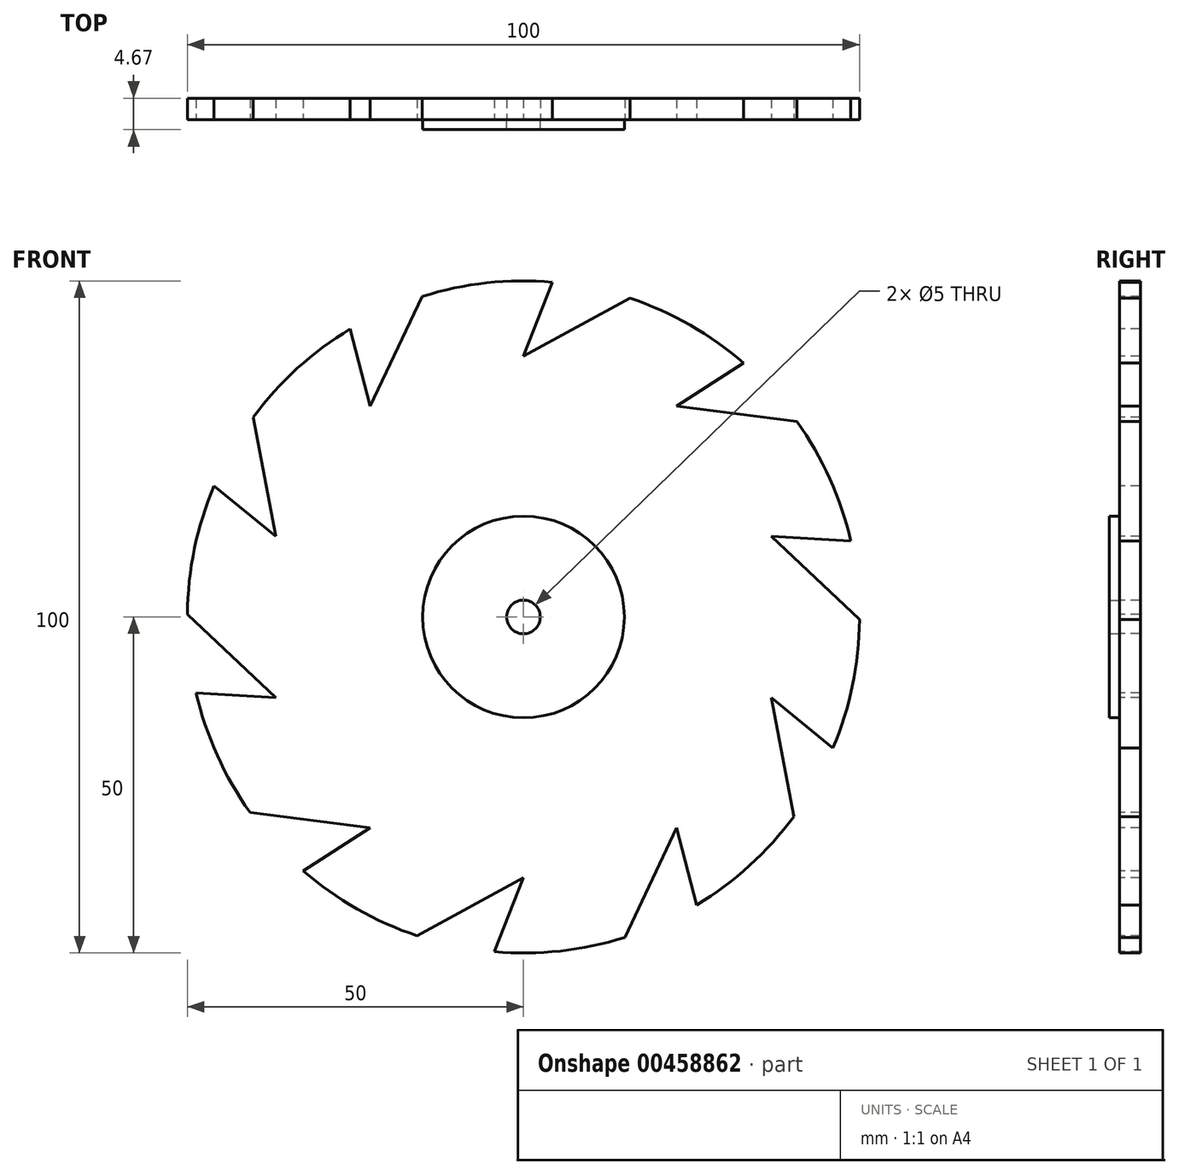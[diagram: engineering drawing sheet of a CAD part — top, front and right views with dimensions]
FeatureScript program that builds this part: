
annotation { "Feature Type Name" : "Feature", "Feature Type Description" : "" }
export const myFeature = defineFeature(function(context is Context, id is Id, definition is map)
    precondition{}
    {
        {
            var Q0;
            Q0=qCreatedBy(makeId("Front.planeOp"),FACE);
            var sketch = newSketch(context, id + "F0", { "sketchPlane" : qUnion([Q0])});
            skCircle(sketch, "E0", {"center": v(0, 0) * mm, "radius": 50 * mm});
            skSolve(sketch);
        }
        {
            var Q0;
            Q0=makeQuery(id+"F0.imprint","IMPRINT",FACE,{"disambiguationData":[TD([[makeQuery(id+"F0.imprint","IMPRINT",EDGE,{"derivedFrom":sQuery(id+"F0.wireOp",EDGE,"E0")}),1.0]])]});
            extrude(context, id + "F1", {"entities" : qUnion([Q0]), "depth" : 3.17 * mm, "offsetDistance" : 25 * mm});
        }
        {
            var Q0;
            Q0=makeQuery(id+"F1.opExtrude","CAP_FACE",FACE,{"disambiguationData":[OSD([sQuery(id+"F0.wireOp",EDGE,"E0")])],"isStart":false});
            var sketch = newSketch(context, id + "F2", { "sketchPlane" : qUnion([Q0])});
            skCircle(sketch, "E1", {"center": v(0, 0) * mm, "radius": 2.5 * mm});
            skSolve(sketch);
        }
        {
            var Q0;
            Q0=makeQuery(id+"F2.imprint","IMPRINT",FACE,{"disambiguationData":[TD([[makeQuery(id+"F2.imprint","IMPRINT",EDGE,{"derivedFrom":sQuery(id+"F2.wireOp",EDGE,"E1")}),1.0]])]});
            extrude(context, id + "F3", {"entities" : qUnion([Q0]), "operationType" : NewBodyOperationType.REMOVE, "oppositeDirection" : true, "depth" : 25 * mm, "offsetDistance" : 25 * mm});
        }
        {
            var Q0;
            Q0=makeQuery(id+"F1.opExtrude","CAP_FACE",FACE,{"disambiguationData":[OSD([sQuery(id+"F0.wireOp",EDGE,"E0")])],"isStart":false});
            var sketch = newSketch(context, id + "F4", { "sketchPlane" : qUnion([Q0])});
            skCircle(sketch, "E2", {"center": v(0, 0) * mm, "radius": 15 * mm});
            skSolve(sketch);
        }
        {
            var Q0;
            Q0=makeQuery(id+"F4.imprint","IMPRINT",FACE,{"disambiguationData":[TD([[makeQuery(id+"F4.imprint","IMPRINT",EDGE,{"derivedFrom":sQuery(id+"F4.wireOp",EDGE,"E2")}),1.0]])]});
            extrude(context, id + "F5", {"entities" : qUnion([Q0]), "depth" : 1.5 * mm, "offsetDistance" : 25 * mm});
        }
        {
            var Q0;
            Q0=makeQuery(id+"F1.opExtrude","CAP_FACE",FACE,{"disambiguationData":[OSD([sQuery(id+"F0.wireOp",EDGE,"E0")])],"isStart":false});
            var sketch = newSketch(context, id + "F6", { "sketchPlane" : qUnion([Q0])});
            skLineSegment(sketch, "E3", {"start": v(15.84, 47.43) * mm, "end": v(0, 38.78) * mm});
            skLineSegment(sketch, "E4", {"start": v(0, 38.78) * mm, "end": v(4.31, 49.81) * mm});
            skLineSegment(sketch, "E5.1.0", {"start": v(-15.06, 47.68) * mm, "end": v(-22.8, 31.37) * mm});
            skLineSegment(sketch, "E5.1.1", {"start": v(-22.8, 31.37) * mm, "end": v(-25.79, 42.84) * mm});
            skLineSegment(sketch, "E5.2.0", {"start": v(-40.2, 29.72) * mm, "end": v(-36.88, 11.98) * mm});
            skLineSegment(sketch, "E5.2.1", {"start": v(-36.88, 11.98) * mm, "end": v(-46.04, 19.5) * mm});
            skLineSegment(sketch, "E5.3.0", {"start": v(-50, 0.4) * mm, "end": v(-36.88, -11.98) * mm});
            skLineSegment(sketch, "E5.3.1", {"start": v(-36.88, -11.98) * mm, "end": v(-48.7, -11.29) * mm});
            skLineSegment(sketch, "E5.4.0", {"start": v(-40.69, -29.06) * mm, "end": v(-22.8, -31.37) * mm});
            skLineSegment(sketch, "E5.4.1", {"start": v(-22.8, -31.37) * mm, "end": v(-32.77, -37.76) * mm});
            skLineSegment(sketch, "E5.5.0", {"start": v(-15.84, -47.43) * mm, "end": v(0, -38.78) * mm});
            skLineSegment(sketch, "E5.5.1", {"start": v(0, -38.78) * mm, "end": v(-4.31, -49.81) * mm});
            skLineSegment(sketch, "E5.6.0", {"start": v(15.06, -47.68) * mm, "end": v(22.8, -31.37) * mm});
            skLineSegment(sketch, "E5.6.1", {"start": v(22.8, -31.37) * mm, "end": v(25.79, -42.84) * mm});
            skLineSegment(sketch, "E5.7.0", {"start": v(40.2, -29.72) * mm, "end": v(36.88, -11.98) * mm});
            skLineSegment(sketch, "E5.7.1", {"start": v(36.88, -11.98) * mm, "end": v(46.04, -19.5) * mm});
            skLineSegment(sketch, "E5.8.0", {"start": v(50, -0.4) * mm, "end": v(36.88, 11.98) * mm});
            skLineSegment(sketch, "E5.8.1", {"start": v(36.88, 11.98) * mm, "end": v(48.7, 11.29) * mm});
            skLineSegment(sketch, "E5.9.0", {"start": v(40.69, 29.06) * mm, "end": v(22.8, 31.37) * mm});
            skLineSegment(sketch, "E5.9.1", {"start": v(22.8, 31.37) * mm, "end": v(32.77, 37.76) * mm});
            skPoint(sketch, "E5.center", {"position": v(0, 0) * mm});
            skSolve(sketch);
        }
        {
            var Q0;
            {var subQ0=sQuery(id+"F6.wireOp",EDGE,"E5.1.0");Q0=makeQuery(id+"F6.imprint","IMPRINT",FACE,{"disambiguationData":[TD([[makeQuery(id+"F6.imprint","IMPRINT",EDGE,{"derivedFrom":subQ0}),-1.0]])]});}
            var Q1;
            {var subQ0=sQuery(id+"F6.wireOp",EDGE,"E3");Q1=makeQuery(id+"F6.imprint","IMPRINT",FACE,{"disambiguationData":[TD([[makeQuery(id+"F6.imprint","IMPRINT",EDGE,{"derivedFrom":subQ0}),-1.0]])]});}
            var Q2;
            {var subQ0=sQuery(id+"F6.wireOp",EDGE,"E5.9.0");Q2=makeQuery(id+"F6.imprint","IMPRINT",FACE,{"disambiguationData":[TD([[makeQuery(id+"F6.imprint","IMPRINT",EDGE,{"derivedFrom":subQ0}),-1.0]])]});}
            var Q3;
            {var subQ0=sQuery(id+"F6.wireOp",EDGE,"E5.8.0");Q3=makeQuery(id+"F6.imprint","IMPRINT",FACE,{"disambiguationData":[TD([[makeQuery(id+"F6.imprint","IMPRINT",EDGE,{"derivedFrom":subQ0}),-1.0]])]});}
            var Q4;
            {var subQ0=sQuery(id+"F6.wireOp",EDGE,"E5.7.0");Q4=makeQuery(id+"F6.imprint","IMPRINT",FACE,{"disambiguationData":[TD([[makeQuery(id+"F6.imprint","IMPRINT",EDGE,{"derivedFrom":subQ0}),-1.0]])]});}
            var Q5;
            {var subQ0=sQuery(id+"F6.wireOp",EDGE,"E5.6.0");Q5=makeQuery(id+"F6.imprint","IMPRINT",FACE,{"disambiguationData":[TD([[makeQuery(id+"F6.imprint","IMPRINT",EDGE,{"derivedFrom":subQ0}),-1.0]])]});}
            var Q6;
            {var subQ0=sQuery(id+"F6.wireOp",EDGE,"E5.5.0");Q6=makeQuery(id+"F6.imprint","IMPRINT",FACE,{"disambiguationData":[TD([[makeQuery(id+"F6.imprint","IMPRINT",EDGE,{"derivedFrom":subQ0}),-1.0]])]});}
            var Q7;
            {var subQ0=sQuery(id+"F6.wireOp",EDGE,"E5.4.0");Q7=makeQuery(id+"F6.imprint","IMPRINT",FACE,{"disambiguationData":[TD([[makeQuery(id+"F6.imprint","IMPRINT",EDGE,{"derivedFrom":subQ0}),-1.0]])]});}
            var Q8;
            {var subQ0=sQuery(id+"F6.wireOp",EDGE,"E5.3.0");Q8=makeQuery(id+"F6.imprint","IMPRINT",FACE,{"disambiguationData":[TD([[makeQuery(id+"F6.imprint","IMPRINT",EDGE,{"derivedFrom":subQ0}),-1.0]])]});}
            var Q9;
            {var subQ0=sQuery(id+"F6.wireOp",EDGE,"E5.2.0");Q9=makeQuery(id+"F6.imprint","IMPRINT",FACE,{"disambiguationData":[TD([[makeQuery(id+"F6.imprint","IMPRINT",EDGE,{"derivedFrom":subQ0}),-1.0]])]});}
            extrude(context, id + "F7", {"entities" : qUnion([Q0, Q1, Q2, Q3, Q4, Q5, Q6, Q7, Q8, Q9]), "operationType" : NewBodyOperationType.REMOVE, "oppositeDirection" : true, "depth" : 25 * mm, "offsetDistance" : 25 * mm});
        }
    });
